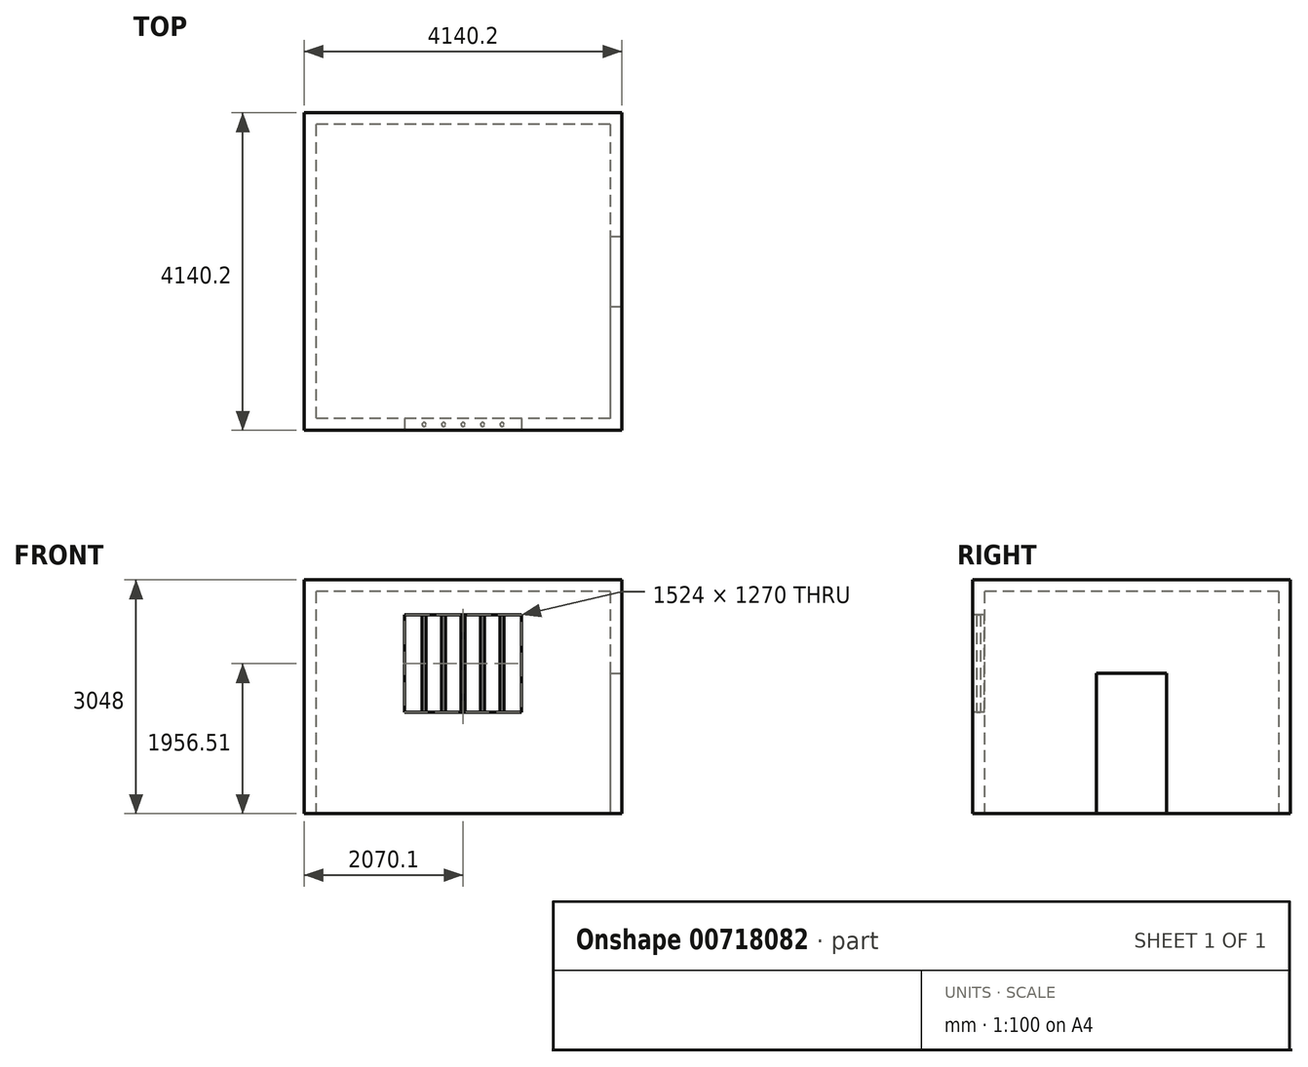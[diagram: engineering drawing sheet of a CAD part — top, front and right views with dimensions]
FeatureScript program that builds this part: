
annotation { "Feature Type Name" : "Feature", "Feature Type Description" : "" }
export const myFeature = defineFeature(function(context is Context, id is Id, definition is map)
    precondition{}
    {
        {
            var Q0;
            Q0=qCreatedBy(makeId("Top.planeOp"),FACE);
            var sketch = newSketch(context, id + "F0", { "sketchPlane" : qUnion([Q0])});
            skLineSegment(sketch, "E0.bottom", {"start": v(2070.1, -2070.1) * mm, "end": v(-2070.1, -2070.1) * mm});
            skLineSegment(sketch, "E0.top", {"start": v(2070.1, 2070.1) * mm, "end": v(-2070.1, 2070.1) * mm});
            skLineSegment(sketch, "E0.left", {"start": v(2070.1, -2070.1) * mm, "end": v(2070.1, 2070.1) * mm});
            skLineSegment(sketch, "E0.right", {"start": v(-2070.1, -2070.1) * mm, "end": v(-2070.1, 2070.1) * mm});
            skPoint(sketch, "E0.middle", {"position": v(0, 0) * mm});
            skSolve(sketch);
        }
        {
            var Q0;
            Q0 = qSketchRegion(id + "F0", true);
            extrude(context, id + "F1", {"entities" : qUnion([Q0]), "depth" : 3048 * mm, "offsetDistance" : 25.4 * mm});
        }
        {
            var Q0;
            Q0=makeQuery(id+"F1.opExtrude","SWEPT_FACE",FACE,{"disambiguationData":[OSD([sQuery(id+"F0.wireOp",EDGE,"E0.bottom")])]});
            var sketch = newSketch(context, id + "F2", { "sketchPlane" : qUnion([Q0])});
            skLineSegment(sketch, "E1.bottom", {"start": v(762, 1321.51) * mm, "end": v(-762, 1321.51) * mm});
            skLineSegment(sketch, "E1.top", {"start": v(762, 2591.51) * mm, "end": v(-762, 2591.51) * mm});
            skLineSegment(sketch, "E1.left", {"start": v(762, 1321.51) * mm, "end": v(762, 2591.51) * mm});
            skLineSegment(sketch, "E1.right", {"start": v(-762, 1321.51) * mm, "end": v(-762, 2591.51) * mm});
            skPoint(sketch, "E1.middle", {"position": v(0, 1956.51) * mm});
            skSolve(sketch);
        }
        {
            var Q0;
            Q0 = qSketchRegion(id + "F2", true);
            extrude(context, id + "F3", {"entities" : qUnion([Q0]), "operationType" : NewBodyOperationType.REMOVE, "oppositeDirection" : true, "depth" : 152.4 * mm, "offsetDistance" : 25.4 * mm});
        }
        {
            var Q0;
            Q0=makeQuery(id+"F1.opExtrude","CAP_FACE",FACE,{"disambiguationData":[OSD([sQuery(id+"F0.wireOp",EDGE,"E0.bottom"),sQuery(id+"F0.wireOp",EDGE,"E0.top"),sQuery(id+"F0.wireOp",EDGE,"E0.left"),sQuery(id+"F0.wireOp",EDGE,"E0.right")])],"isStart":true});
            var sketch = newSketch(context, id + "F4", { "sketchPlane" : qUnion([Q0])});
            skLineSegment(sketch, "E2.bottom", {"start": v(1917.7, -1917.7) * mm, "end": v(-1917.7, -1917.7) * mm});
            skLineSegment(sketch, "E2.top", {"start": v(1917.7, 1917.7) * mm, "end": v(-1917.7, 1917.7) * mm});
            skLineSegment(sketch, "E2.left", {"start": v(1917.7, -1917.7) * mm, "end": v(1917.7, 1917.7) * mm});
            skLineSegment(sketch, "E2.right", {"start": v(-1917.7, -1917.7) * mm, "end": v(-1917.7, 1917.7) * mm});
            skPoint(sketch, "E2.middle", {"position": v(0, 0) * mm});
            skSolve(sketch);
        }
        {
            var Q0;
            Q0 = qSketchRegion(id + "F4", true);
            extrude(context, id + "F5", {"entities" : qUnion([Q0]), "operationType" : NewBodyOperationType.REMOVE, "oppositeDirection" : true, "depth" : 2895.6 * mm, "offsetDistance" : 25.4 * mm});
        }
        {
            var Q0;
            Q0=makeQuery(id+"F3.boolean.opBoolean","COPY",FACE,{"derivedFrom":makeQuery(id+"F3.opExtrude","SWEPT_FACE",FACE,{"disambiguationData":[OSD([sQuery(id+"F2.wireOp",EDGE,"E1.bottom")])]})});
            var sketch = newSketch(context, id + "F6", { "sketchPlane" : qUnion([Q0])});
            skCircle(sketch, "E3", {"center": v(-508, -1993.9) * mm, "radius": 25.4 * mm});
            skPoint(sketch, "E3.centerSnap0", {"position": v(-762, -1993.9) * mm});
            skCircle(sketch, "E4", {"center": v(0, -1993.9) * mm, "radius": 25.4 * mm});
            skCircle(sketch, "E5", {"center": v(508, -1993.9) * mm, "radius": 25.4 * mm});
            skCircle(sketch, "E6", {"center": v(-254, -1993.9) * mm, "radius": 25.4 * mm});
            skCircle(sketch, "E7", {"center": v(254, -1993.9) * mm, "radius": 25.4 * mm});
            skSolve(sketch);
        }
        {
            var Q0;
            Q0 = qSketchRegion(id + "F6", true);
            extrude(context, id + "F7", {"entities" : qUnion([Q0]), "operationType" : NewBodyOperationType.ADD, "depth" : 1270 * mm, "offsetDistance" : 25.4 * mm});
        }
        {
            var Q0;
            Q0=makeQuery(id+"F1.opExtrude","SWEPT_FACE",FACE,{"disambiguationData":[OSD([sQuery(id+"F0.wireOp",EDGE,"E0.left")])]});
            var sketch = newSketch(context, id + "F8", { "sketchPlane" : qUnion([Q0])});
            skLineSegment(sketch, "E8.bottom", {"start": v(457.2, 1828.8) * mm, "end": v(-457.2, 1828.8) * mm});
            skLineSegment(sketch, "E8.top", {"start": v(457.2, -1828.8) * mm, "end": v(-457.2, -1828.8) * mm});
            skLineSegment(sketch, "E8.left", {"start": v(457.2, 1828.8) * mm, "end": v(457.2, -1828.8) * mm});
            skLineSegment(sketch, "E8.right", {"start": v(-457.2, 1828.8) * mm, "end": v(-457.2, -1828.8) * mm});
            skPoint(sketch, "E8.middle", {"position": v(0, 0) * mm});
            skSolve(sketch);
        }
        {
            var Q0;
            Q0 = qSketchRegion(id + "F8", true);
            extrude(context, id + "F9", {"entities" : qUnion([Q0]), "operationType" : NewBodyOperationType.REMOVE, "oppositeDirection" : true, "depth" : 152.4 * mm, "offsetDistance" : 25.4 * mm});
        }
    });
